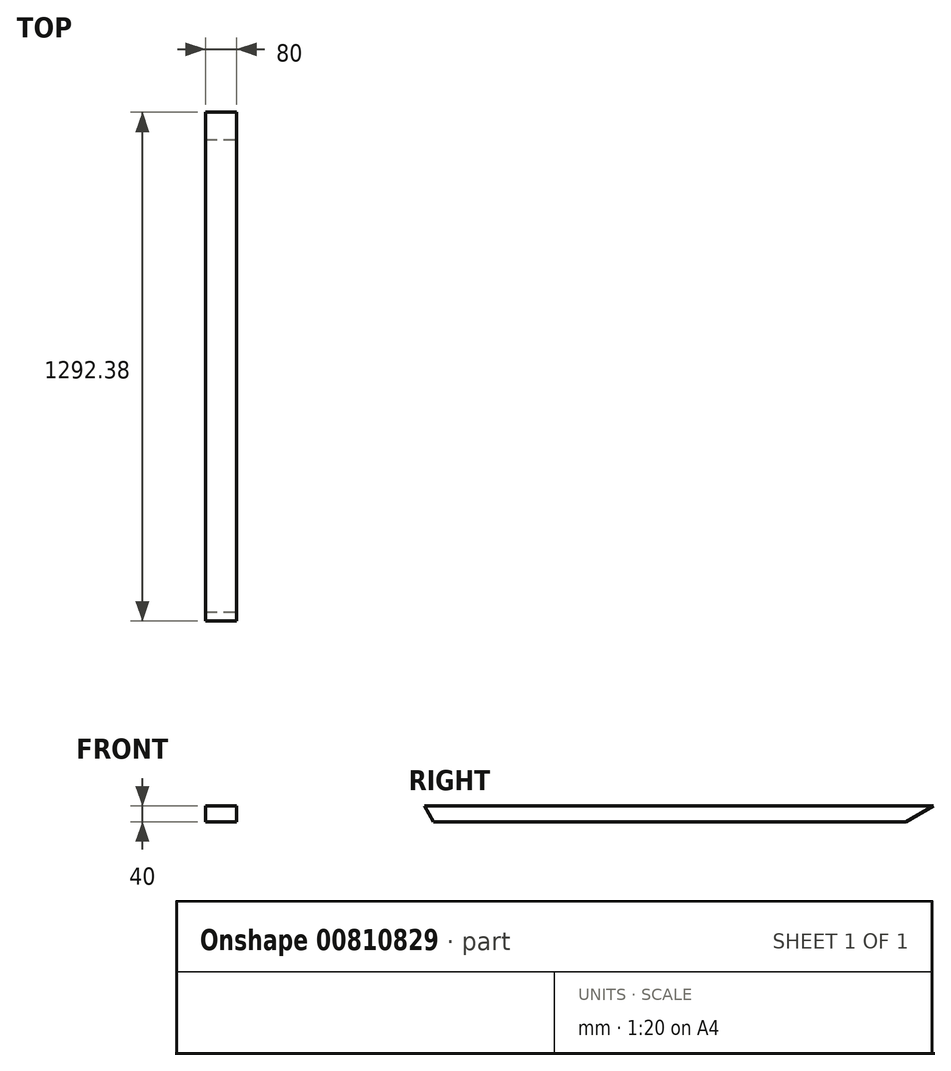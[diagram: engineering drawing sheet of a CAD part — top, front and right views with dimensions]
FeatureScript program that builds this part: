
annotation { "Feature Type Name" : "Feature", "Feature Type Description" : "" }
export const myFeature = defineFeature(function(context is Context, id is Id, definition is map)
    precondition{}
    {
        {
            var Q0;
            Q0=qCreatedBy(makeId("Front.planeOp"),FACE);
            var sketch = newSketch(context, id + "F0", { "sketchPlane" : qUnion([Q0])});
            skLineSegment(sketch, "E0.bottom", {"start": v(40, -20) * mm, "end": v(-40, -20) * mm});
            skLineSegment(sketch, "E0.top", {"start": v(40, 20) * mm, "end": v(-40, 20) * mm});
            skLineSegment(sketch, "E0.left", {"start": v(40, -20) * mm, "end": v(40, 20) * mm});
            skLineSegment(sketch, "E0.right", {"start": v(-40, -20) * mm, "end": v(-40, 20) * mm});
            skPoint(sketch, "E0.middle", {"position": v(0, 0) * mm});
            skSolve(sketch);
        }
        {
            var Q0;
            Q0=makeQuery(id+"F0.imprint","IMPRINT",FACE,{"disambiguationData":[TD([[makeQuery(id+"F0.imprint","IMPRINT",EDGE,{"derivedFrom":sQuery(id+"F0.wireOp",EDGE,"E0.bottom")}),-1.0]])]});
            extrude(context, id + "F1", {"entities" : qUnion([Q0]), "endBound" : BoundingType.SYMMETRIC, "depth" : 1292.37 * mm, "offsetDistance" : 25 * mm});
        }
        {
            var Q0;
            Q0=makeQuery(id+"F1.opExtrude","SWEPT_FACE",FACE,{"disambiguationData":[OSD([sQuery(id+"F0.wireOp",EDGE,"E0.left")])]});
            var sketch = newSketch(context, id + "F2", { "sketchPlane" : qUnion([Q0])});
            skLineSegment(sketch, "E1", {"start": v(646.19, 20) * mm, "end": v(576.9, -20) * mm});
            skLineSegment(sketch, "E2", {"start": v(576.9, -20) * mm, "end": v(646.19, -20) * mm});
            skLineSegment(sketch, "E3", {"start": v(646.19, -20) * mm, "end": v(646.19, 20) * mm});
            skSolve(sketch);
        }
        {
            var Q0;
            Q0=makeQuery(id+"F2.imprint","IMPRINT",FACE,{"disambiguationData":[TD([[makeQuery(id+"F2.imprint","IMPRINT",EDGE,{"derivedFrom":sQuery(id+"F2.wireOp",EDGE,"E1")}),1.0]])]});
            extrude(context, id + "F3", {"entities" : qUnion([Q0]), "operationType" : NewBodyOperationType.REMOVE, "endBound" : BoundingType.THROUGH_ALL, "oppositeDirection" : true, "depth" : 25 * mm, "offsetDistance" : 25 * mm});
        }
        {
            var Q0;
            Q0=makeQuery(id+"F1.opExtrude","SWEPT_FACE",FACE,{"disambiguationData":[OSD([sQuery(id+"F0.wireOp",EDGE,"E0.left")])]});
            var sketch = newSketch(context, id + "F4", { "sketchPlane" : qUnion([Q0])});
            skLineSegment(sketch, "E4", {"start": v(-646.19, 20) * mm, "end": v(-623.1, -20) * mm});
            skLineSegment(sketch, "E5", {"start": v(-646.19, 20) * mm, "end": v(-646.19, -20) * mm});
            skLineSegment(sketch, "E6", {"start": v(-646.19, -20) * mm, "end": v(-623.1, -20) * mm});
            skSolve(sketch);
        }
        {
            var Q0;
            Q0=makeQuery(id+"F4.imprint","IMPRINT",FACE,{"disambiguationData":[TD([[makeQuery(id+"F4.imprint","IMPRINT",EDGE,{"derivedFrom":sQuery(id+"F4.wireOp",EDGE,"E4")}),-1.0]])]});
            extrude(context, id + "F5", {"entities" : qUnion([Q0]), "operationType" : NewBodyOperationType.REMOVE, "endBound" : BoundingType.THROUGH_ALL, "oppositeDirection" : true, "depth" : 25 * mm, "offsetDistance" : 25 * mm});
        }
    });
